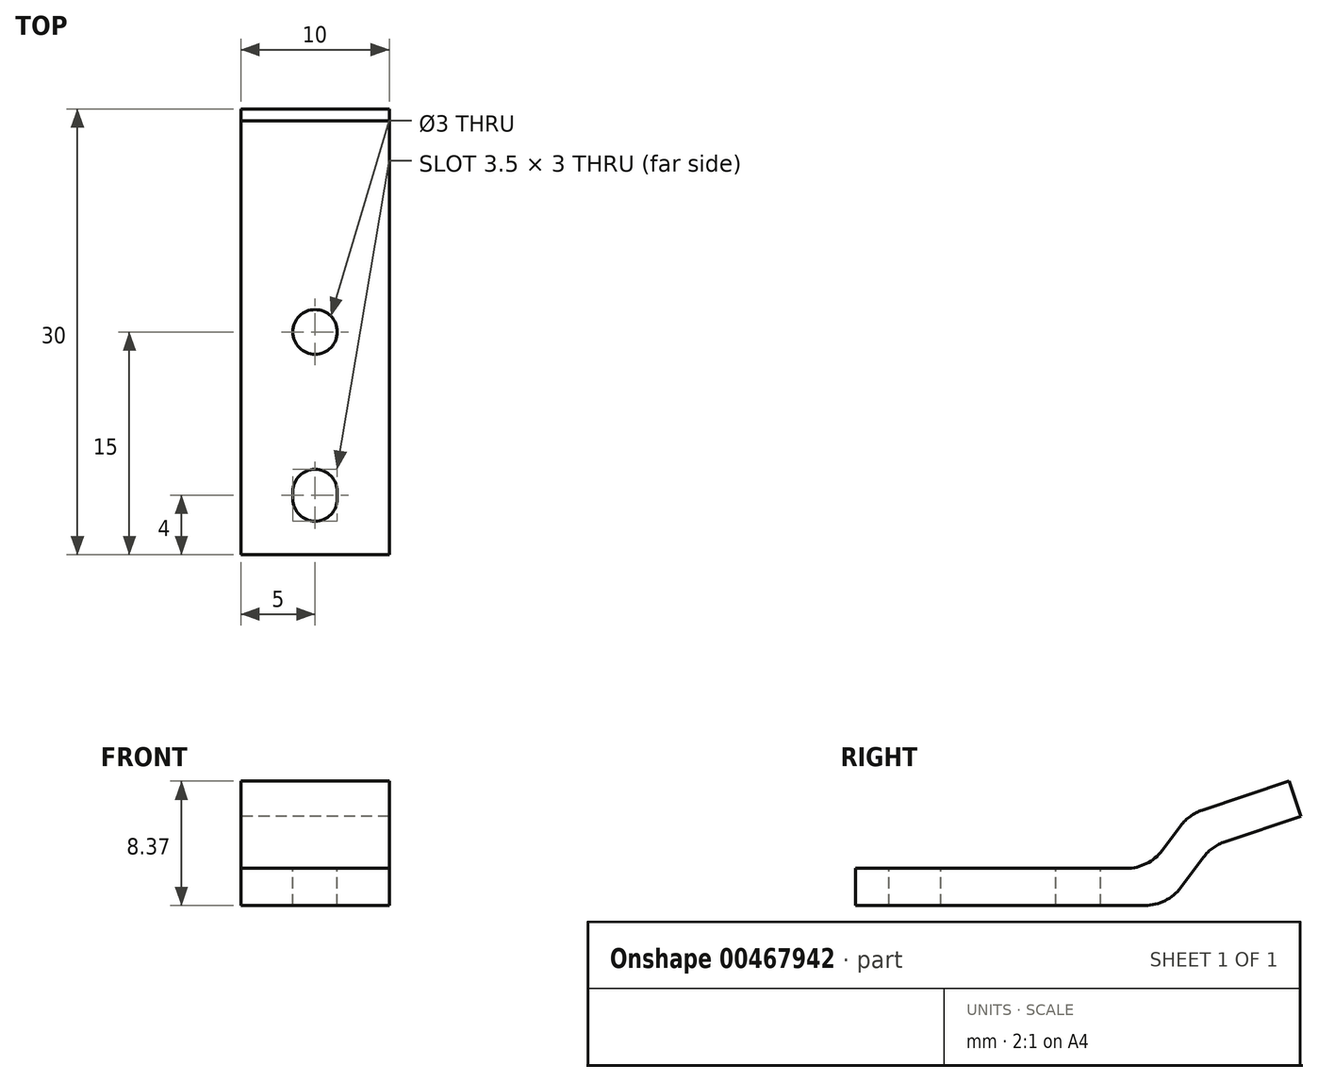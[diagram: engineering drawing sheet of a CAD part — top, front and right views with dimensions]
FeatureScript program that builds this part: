
annotation { "Feature Type Name" : "Feature", "Feature Type Description" : "" }
export const myFeature = defineFeature(function(context is Context, id is Id, definition is map)
    precondition{}
    {
        {
            var Q0;
            Q0=qCreatedBy(makeId("Right.planeOp"),FACE);
            var sketch = newSketch(context, id + "F0", { "sketchPlane" : qUnion([Q0])});
            skLineSegment(sketch, "E0", {"start": v(0, 0) * mm, "end": v(21, 0) * mm});
            skLineSegment(sketch, "E1", {"start": v(21, 0) * mm, "end": v(24, 4) * mm});
            skLineSegment(sketch, "E2", {"start": v(24, 4) * mm, "end": v(30, 6) * mm});
            skLineSegment(sketch, "E3", {"start": v(0, 0) * mm, "end": v(0, 2.5) * mm});
            skLineSegment(sketch, "E4", {"start": v(24, 4) * mm, "end": v(22, 5.5) * mm});
            skLineSegment(sketch, "E5", {"start": v(22, 5.5) * mm, "end": v(19.75, 2.5) * mm});
            skLineSegment(sketch, "E6", {"start": v(0, 2.5) * mm, "end": v(19.75, 2.5) * mm});
            skLineSegment(sketch, "E7", {"start": v(30, 6) * mm, "end": v(29.2, 8.37) * mm});
            skLineSegment(sketch, "E8", {"start": v(29.2, 8.37) * mm, "end": v(22.47, 6.12) * mm});
            skLineSegment(sketch, "E9", {"start": v(22, 5.5) * mm, "end": v(22.47, 6.12) * mm});
            skSolve(sketch);
        }
        {
            var Q0;
            Q0=makeQuery(id+"F0.imprint","IMPRINT",FACE,{"disambiguationData":[TD([[makeQuery(id+"F0.imprint","IMPRINT",EDGE,{"derivedFrom":sQuery(id+"F0.wireOp",EDGE,"E0")}),1.0]])]});
            var Q1;
            Q1=makeQuery(id+"F0.imprint","IMPRINT",FACE,{"disambiguationData":[TD([[makeQuery(id+"F0.imprint","IMPRINT",EDGE,{"derivedFrom":sQuery(id+"F0.wireOp",EDGE,"E2")}),1.0]])]});
            extrude(context, id + "F1", {"entities" : qUnion([Q0, Q1]), "depth" : 5 * mm, "hasSecondDirection" : true, "secondDirectionOppositeDirection" : true, "secondDirectionDepth" : 5 * mm});
        }
        {
            var Q0;
            Q0=makeQuery(id+"F1.opExtrude","SWEPT_EDGE",EDGE,{"disambiguationData":[OSD([sQuery(id+"F0.wireOp",EDGE,"E0"),sQuery(id+"F0.wireOp",EDGE,"E1")])]});
            var Q1;
            Q1=makeQuery(id+"F1.opExtrude","SWEPT_EDGE",EDGE,{"disambiguationData":[OSD([sQuery(id+"F0.wireOp",EDGE,"E5"),sQuery(id+"F0.wireOp",EDGE,"E6")])]});
            fillet(context, id + "F2", {"entities" : qUnion([Q0, Q1]), "radius" : 3 * mm, "tangentPropagation" : true, "allowEdgeOverflow" : false});
        }
        {
            var Q0;
            Q0=makeQuery(id+"F1.opExtrude","SWEPT_EDGE",EDGE,{"disambiguationData":[OSD([sQuery(id+"F0.wireOp",EDGE,"E8"),sQuery(id+"F0.wireOp",EDGE,"E9")])]});
            var Q1;
            Q1=makeQuery(id+"F1.opExtrude","SWEPT_EDGE",EDGE,{"disambiguationData":[OSD([sQuery(id+"F0.wireOp",EDGE,"E1"),sQuery(id+"F0.wireOp",EDGE,"E2"),sQuery(id+"F0.wireOp",EDGE,"E4")])]});
            fillet(context, id + "F3", {"entities" : qUnion([Q0, Q1]), "radius" : 3 * mm, "tangentPropagation" : true, "allowEdgeOverflow" : false});
        }
        {
            var Q0;
            Q0=makeQuery(id+"F1.opExtrude","SWEPT_FACE",FACE,{"disambiguationData":[OSD([sQuery(id+"F0.wireOp",EDGE,"E6")])]});
            var sketch = newSketch(context, id + "F4", { "sketchPlane" : qUnion([Q0])});
            skCircle(sketch, "E10", {"center": v(0, 15) * mm, "radius": 1.5 * mm});
            skPoint(sketch, "E10.centerSnap0", {"position": v(0, 0) * mm});
            skCircle(sketch, "E11", {"center": v(0, 4) * mm, "radius": 1.5 * mm});
            skPoint(sketch, "E12", {"position": v(0, 4.25) * mm});
            skPoint(sketch, "E13", {"position": v(0, 3.75) * mm});
            skCircle(sketch, "E14", {"center": v(0, 4.25) * mm, "radius": 1.5 * mm});
            skCircle(sketch, "E15", {"center": v(0, 3.75) * mm, "radius": 1.5 * mm});
            skLineSegment(sketch, "E16", {"start": v(-1.5, 4) * mm, "end": v(-1.5, 4.25) * mm});
            skLineSegment(sketch, "E17", {"start": v(-1.5, 4) * mm, "end": v(-1.5, 3.75) * mm});
            skLineSegment(sketch, "E18", {"start": v(1.5, 4) * mm, "end": v(1.5, 4.25) * mm});
            skLineSegment(sketch, "E19", {"start": v(1.5, 4) * mm, "end": v(1.5, 3.75) * mm});
            skSolve(sketch);
        }
        {
            var Q0;
            Q0=makeQuery(id+"F4.imprint","IMPRINT",FACE,{"disambiguationData":[TD([[makeQuery(id+"F4.imprint","IMPRINT",EDGE,{"derivedFrom":sQuery(id+"F4.wireOp",EDGE,"E10")}),1.0]])]});
            var Q1;
            Q1=makeQuery(id+"F4.imprint","IMPRINT",FACE,{"disambiguationData":[TD([[makeQuery(id+"F4.imprint","IMPRINT",EDGE,{"derivedFrom":sQuery(id+"F4.wireOp",EDGE,"E11")}),1.0]])]});
            var Q2;
            {var subQ0=sQuery(id+"F4.wireOp",EDGE,"E15");var subQ1=sQuery(id+"F4.wireOp",EDGE,"E14");var subQ2=makeQuery(id+"F4.imprint","INTERSECT",VERTEX,{"disambiguationData":[OD(0.0)],"derivedFrom":[subQ1,subQ0]});Q2=makeQuery(id+"F4.imprint","IMPRINT",FACE,{"disambiguationData":[TD([[makeQuery(id+"F4.imprint","IMPRINT",EDGE,{"disambiguationData":[TD([[subQ2,-1.0]])],"derivedFrom":subQ1}),1.0]])]});}
            var Q3;
            {var subQ0=sQuery(id+"F4.wireOp",EDGE,"E14");var subQ1=sQuery(id+"F4.wireOp",EDGE,"E11");var subQ2=makeQuery(id+"F4.imprint","INTERSECT",VERTEX,{"disambiguationData":[OD(0.0)],"derivedFrom":[subQ1,subQ0]});Q3=makeQuery(id+"F4.imprint","IMPRINT",FACE,{"disambiguationData":[TD([[makeQuery(id+"F4.imprint","IMPRINT",EDGE,{"disambiguationData":[TD([[subQ2,-1.0]])],"derivedFrom":subQ1}),1.0]])]});}
            var Q4;
            {var subQ0=sQuery(id+"F4.wireOp",EDGE,"E14");var subQ1=sQuery(id+"F4.wireOp",EDGE,"E11");var subQ2=makeQuery(id+"F4.imprint","INTERSECT",VERTEX,{"disambiguationData":[OD(0.0)],"derivedFrom":[subQ1,subQ0]});Q4=makeQuery(id+"F4.imprint","IMPRINT",FACE,{"disambiguationData":[TD([[makeQuery(id+"F4.imprint","IMPRINT",EDGE,{"disambiguationData":[TD([[subQ2,-1.0]])],"derivedFrom":subQ1}),-1.0]])]});}
            var Q5;
            {var subQ0=sQuery(id+"F4.wireOp",EDGE,"E15");var subQ1=sQuery(id+"F4.wireOp",EDGE,"E11");var subQ2=makeQuery(id+"F4.imprint","INTERSECT",VERTEX,{"disambiguationData":[OD(0.0)],"derivedFrom":[subQ1,subQ0]});Q5=makeQuery(id+"F4.imprint","IMPRINT",FACE,{"disambiguationData":[TD([[makeQuery(id+"F4.imprint","IMPRINT",EDGE,{"disambiguationData":[TD([[subQ2,-1.0]])],"derivedFrom":subQ1}),1.0]])]});}
            var Q6;
            {var subQ0=sQuery(id+"F4.wireOp",EDGE,"E15");var subQ1=sQuery(id+"F4.wireOp",EDGE,"E11");var subQ2=makeQuery(id+"F4.imprint","INTERSECT",VERTEX,{"disambiguationData":[OD(0.0)],"derivedFrom":[subQ1,subQ0]});Q6=makeQuery(id+"F4.imprint","IMPRINT",FACE,{"disambiguationData":[TD([[makeQuery(id+"F4.imprint","IMPRINT",EDGE,{"disambiguationData":[TD([[subQ2,-1.0]])],"derivedFrom":subQ1}),-1.0]])]});}
            var Q7;
            {var subQ0=sQuery(id+"F4.wireOp",EDGE,"E18");Q7=makeQuery(id+"F4.imprint","IMPRINT",FACE,{"disambiguationData":[TD([[makeQuery(id+"F4.imprint","IMPRINT",EDGE,{"derivedFrom":subQ0}),1.0]])]});}
            var Q8;
            {var subQ0=sQuery(id+"F4.wireOp",EDGE,"E19");Q8=makeQuery(id+"F4.imprint","IMPRINT",FACE,{"disambiguationData":[TD([[makeQuery(id+"F4.imprint","IMPRINT",EDGE,{"derivedFrom":subQ0}),-1.0]])]});}
            var Q9;
            {var subQ0=sQuery(id+"F4.wireOp",EDGE,"E16");Q9=makeQuery(id+"F4.imprint","IMPRINT",FACE,{"disambiguationData":[TD([[makeQuery(id+"F4.imprint","IMPRINT",EDGE,{"derivedFrom":subQ0}),-1.0]])]});}
            var Q10;
            {var subQ0=sQuery(id+"F4.wireOp",EDGE,"E17");Q10=makeQuery(id+"F4.imprint","IMPRINT",FACE,{"disambiguationData":[TD([[makeQuery(id+"F4.imprint","IMPRINT",EDGE,{"derivedFrom":subQ0}),1.0]])]});}
            extrude(context, id + "F5", {"entities" : qUnion([Q0, Q1, Q2, Q3, Q4, Q5, Q6, Q7, Q8, Q9, Q10]), "operationType" : NewBodyOperationType.REMOVE, "endBound" : BoundingType.UP_TO_NEXT, "oppositeDirection" : true, "depth" : 25 * mm});
        }
    });
